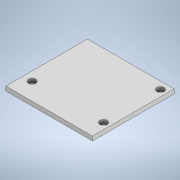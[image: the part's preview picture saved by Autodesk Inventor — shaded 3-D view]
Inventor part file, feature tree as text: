
AUTODESK INVENTOR PART (.ipt)
format: ipt  version: 2020 (Build 240168000, 168)  size: 109,568 bytes
history: native  units: in
note: dims shown in document units (in); Inventor stores cm internally (conversion verified against a paired STEP export)
features: extrude x1, sketch x1
ambient origin geometry x8: Origin, YZ Plane, XZ Plane, XY Plane, X Axis, Y Axis, Z Axis, Center Point
bodies: Body1 (feature_tree)
feature tree (2):
  extrude  "Extrusion2"  Depth=1.405in
  sketch  "Sketch1"  dims[d15=1.325in d16=1.405in d17=0.1in d18=0.12in d19=0.119in d20=0.925in d21=1.16in d22=0.119in d23=0.07in d24=0.0in d27=0.5in d28=0.0344in d29=0.5in d30=0.0344in]
